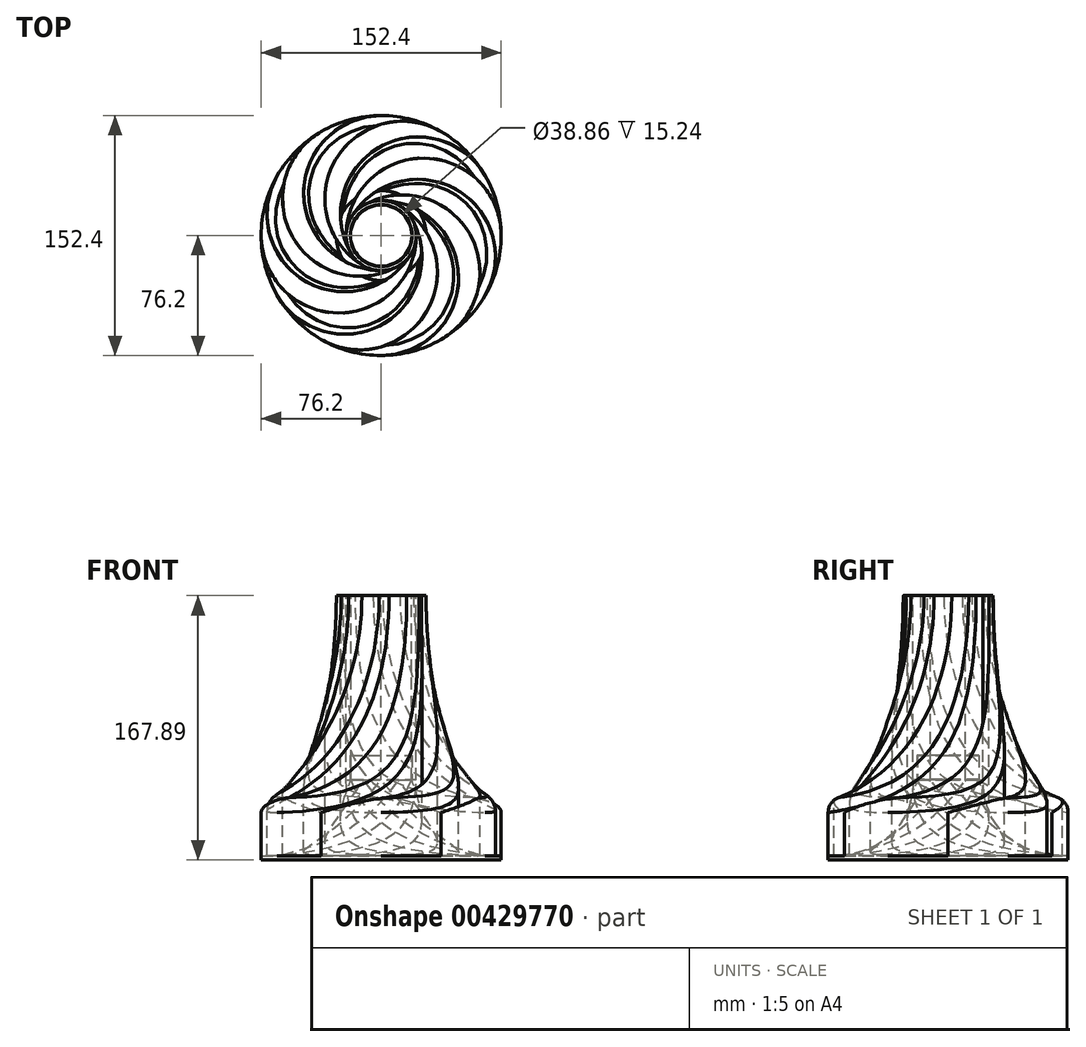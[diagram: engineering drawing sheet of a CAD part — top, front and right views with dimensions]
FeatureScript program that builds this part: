
annotation { "Feature Type Name" : "Feature", "Feature Type Description" : "" }
export const myFeature = defineFeature(function(context is Context, id is Id, definition is map)
    precondition{}
    {
        {
            var Q0;
            Q0=qCreatedBy(makeId("Front.planeOp"),FACE);
            var sketch = newSketch(context, id + "F0", { "sketchPlane" : qUnion([Q0])});
            skLineSegment(sketch, "E0", {"start": v(0, 0) * mm, "end": v(19.68, 0) * mm});
            skLineSegment(sketch, "E1", {"start": v(0, 0) * mm, "end": v(-19.69, 0) * mm});
            skLineSegment(sketch, "E2", {"start": v(19.68, 0) * mm, "end": v(19.68, 15.5) * mm});
            skLineSegment(sketch, "E3", {"start": v(-19.69, 0) * mm, "end": v(-19.69, 15.5) * mm});
            skLineSegment(sketch, "E4", {"start": v(19.68, 15.5) * mm, "end": v(19.43, 15.5) * mm});
            skLineSegment(sketch, "E5", {"start": v(0, 0) * mm, "end": v(0, 0.25) * mm});
            skLineSegment(sketch, "E6", {"start": v(0, 0.25) * mm, "end": v(19.43, 0.25) * mm});
            skLineSegment(sketch, "E7", {"start": v(19.43, 0.25) * mm, "end": v(19.43, 15.5) * mm});
            skLineSegment(sketch, "E8", {"start": v(-19.69, 15.5) * mm, "end": v(-19.43, 15.5) * mm});
            skLineSegment(sketch, "E9", {"start": v(-19.43, 15.5) * mm, "end": v(-19.43, 0.25) * mm});
            skLineSegment(sketch, "E10", {"start": v(-19.43, 0.25) * mm, "end": v(0, 0.25) * mm});
            skSolve(sketch);
        }
        {
            var Q0;
            Q0=makeQuery(id+"F0.imprint","IMPRINT",FACE,{"disambiguationData":[TD([[makeQuery(id+"F0.imprint","IMPRINT",EDGE,{"derivedFrom":sQuery(id+"F0.wireOp",EDGE,"E1")}),-1.0]])]});
            var Q1;
            Q1=sQuery(id+"F0.wireOp",EDGE,"E5");
            revolve(context, id + "F1", {"entities" : qUnion([Q0]), "axis" : qUnion([Q1]), "revolveType" : RevolveType.FULL});
        }
        {
            var Q0;
            Q0=qCreatedBy(makeId("Front.planeOp"),FACE);
            var sketch = newSketch(context, id + "F2", { "sketchPlane" : qUnion([Q0])});
            skLineSegment(sketch, "E11.0", {"start": v(-22.23, 0) * mm, "end": v(-22.23, 15.5) * mm});
            skLineSegment(sketch, "E12", {"start": v(-22.23, 0) * mm, "end": v(0, 0) * mm});
            skLineSegment(sketch, "E13", {"start": v(0, 0) * mm, "end": v(0, -50.8) * mm});
            skLineSegment(sketch, "E14", {"start": v(0, -50.8) * mm, "end": v(-76.2, -50.8) * mm});
            skLineSegment(sketch, "E15", {"start": v(-22.23, 15.5) * mm, "end": v(-22.23, 117.1) * mm});
            skLineSegment(sketch, "E16", {"start": v(-22.23, 117.1) * mm, "end": v(-28.58, 117.1) * mm});
            skLineSegment(sketch, "E17", {"start": v(-76.2, -50.8) * mm, "end": v(-76.2, -12.7) * mm});
            skFitSpline(sketch, "E18", {"points": [v(-28.58, 117.1) * mm, v(-76.2, -12.7) * mm], "startDerivative": vector(0, -266.32) * mm, "endDerivative": vector(-55.61, 0) * mm});
            skSolve(sketch);
        }
        {
            var Q0;
            Q0=makeQuery(id+"F2.imprint","IMPRINT",FACE,{"disambiguationData":[TD([[makeQuery(id+"F2.imprint","IMPRINT",EDGE,{"derivedFrom":sQuery(id+"F2.wireOp",EDGE,"E11.0")}),1.0]])]});
            var Q1;
            Q1=sQuery(id+"F2.wireOp",EDGE,"E13");
            revolve(context, id + "F3", {"entities" : qUnion([Q0]), "axis" : qUnion([Q1]), "revolveType" : RevolveType.FULL});
        }
        {
            var Q0;
            Q0=qCreatedBy(makeId("Top.planeOp"),FACE);
            var sketch = newSketch(context, id + "F4", { "sketchPlane" : qUnion([Q0])});
            skCircle(sketch, "E19.0", {"center": v(0, 0) * mm, "radius": 19.69 * mm});
            skCircle(sketch, "E19.1", {"center": v(0, 0) * mm, "radius": 76.2 * mm});
            skCircle(sketch, "E20.0", {"center": v(0, 0) * mm, "radius": 22.23 * mm});
            skArc(sketch, "E21", {"start": v(0, -76.2) * mm, "mid": v(49.21, -26.99) * mm, "end": v(0, 22.22) * mm});
            skArc(sketch, "E22.1.0", {"start": v(-38.1, -66) * mm, "mid": v(29.13, -47.98) * mm, "end": v(11.11, 19.25) * mm});
            skArc(sketch, "E22.2.0", {"start": v(-66, -38.1) * mm, "mid": v(1.23, -56.11) * mm, "end": v(19.25, 11.11) * mm});
            skArc(sketch, "E22.3.0", {"start": v(-76.2, 0) * mm, "mid": v(-26.99, -49.21) * mm, "end": v(22.22, 0) * mm});
            skArc(sketch, "E22.4.0", {"start": v(-66, 38.1) * mm, "mid": v(-47.98, -29.13) * mm, "end": v(19.25, -11.11) * mm});
            skArc(sketch, "E22.5.0", {"start": v(-38.1, 66) * mm, "mid": v(-56.11, -1.23) * mm, "end": v(11.11, -19.25) * mm});
            skArc(sketch, "E22.6.0", {"start": v(0, 76.2) * mm, "mid": v(-49.21, 26.99) * mm, "end": v(0, -22.22) * mm});
            skArc(sketch, "E22.7.0", {"start": v(38.1, 66) * mm, "mid": v(-29.13, 47.98) * mm, "end": v(-11.11, -19.25) * mm});
            skArc(sketch, "E22.8.0", {"start": v(66, 38.1) * mm, "mid": v(-1.23, 56.11) * mm, "end": v(-19.25, -11.11) * mm});
            skArc(sketch, "E22.9.0", {"start": v(76.2, 0) * mm, "mid": v(26.99, 49.21) * mm, "end": v(-22.22, 0) * mm});
            skArc(sketch, "E22.10.0", {"start": v(66, -38.1) * mm, "mid": v(47.98, 29.13) * mm, "end": v(-19.25, 11.11) * mm});
            skArc(sketch, "E22.11.0", {"start": v(38.1, -66) * mm, "mid": v(56.11, 1.23) * mm, "end": v(-11.11, 19.25) * mm});
            skLineSegment(sketch, "E22.anchor1", {"start": v(0, 0) * mm, "end": v(0, -76.2) * mm, "construction": true});
            skLineSegment(sketch, "E22.anchor2", {"start": v(0, 0) * mm, "end": v(0, -76.2) * mm, "construction": true});
            skSolve(sketch);
        }
        {
            var Q0;
            {var subQ0=sQuery(id+"F4.wireOp",EDGE,"E22.1.0");Q0=makeQuery(id+"F4.imprint","IMPRINT",FACE,{"disambiguationData":[TD([[makeQuery(id+"F4.imprint","IMPRINT",EDGE,{"derivedFrom":subQ0}),1.0]])]});}
            var Q1;
            {var subQ0=sQuery(id+"F4.wireOp",EDGE,"E22.11.0");Q1=makeQuery(id+"F4.imprint","IMPRINT",FACE,{"disambiguationData":[TD([[makeQuery(id+"F4.imprint","IMPRINT",EDGE,{"derivedFrom":subQ0}),1.0]])]});}
            var Q2;
            {var subQ0=sQuery(id+"F4.wireOp",EDGE,"E22.9.0");Q2=makeQuery(id+"F4.imprint","IMPRINT",FACE,{"disambiguationData":[TD([[makeQuery(id+"F4.imprint","IMPRINT",EDGE,{"derivedFrom":subQ0}),1.0]])]});}
            var Q3;
            {var subQ0=sQuery(id+"F4.wireOp",EDGE,"E22.7.0");Q3=makeQuery(id+"F4.imprint","IMPRINT",FACE,{"disambiguationData":[TD([[makeQuery(id+"F4.imprint","IMPRINT",EDGE,{"derivedFrom":subQ0}),1.0]])]});}
            var Q4;
            {var subQ0=sQuery(id+"F4.wireOp",EDGE,"E22.5.0");Q4=makeQuery(id+"F4.imprint","IMPRINT",FACE,{"disambiguationData":[TD([[makeQuery(id+"F4.imprint","IMPRINT",EDGE,{"derivedFrom":subQ0}),1.0]])]});}
            var Q5;
            {var subQ0=sQuery(id+"F4.wireOp",EDGE,"E22.3.0");Q5=makeQuery(id+"F4.imprint","IMPRINT",FACE,{"disambiguationData":[TD([[makeQuery(id+"F4.imprint","IMPRINT",EDGE,{"derivedFrom":subQ0}),1.0]])]});}
            extrude(context, id + "F5", {"entities" : qUnion([Q0, Q1, Q2, Q3, Q4, Q5]), "operationType" : NewBodyOperationType.REMOVE, "endBound" : BoundingType.SYMMETRIC, "oppositeDirection" : true, "depth" : 304.8 * mm});
        }
        {
            var Q0;
            Q0=qCreatedBy(makeId("Front.planeOp"),FACE);
            var sketch = newSketch(context, id + "F6", { "sketchPlane" : qUnion([Q0])});
            skLineSegment(sketch, "E23.0", {"start": v(-22.23, 0) * mm, "end": v(0, 0) * mm});
            skLineSegment(sketch, "E23.1", {"start": v(0, 0) * mm, "end": v(0, -50.8) * mm});
            skLineSegment(sketch, "E23.2", {"start": v(0, -50.8) * mm, "end": v(-76.2, -50.8) * mm});
            skPoint(sketch, "E24", {"position": v(0, -25.4) * mm});
            skLineSegment(sketch, "E25", {"start": v(-76.2, -50.8) * mm, "end": v(-76.2, -48.26) * mm});
            skFitSpline(sketch, "E26", {"points": [v(-22.23, 0) * mm, v(-76.2, -48.26) * mm], "startDerivative": vector(0, -76.2) * mm, "endDerivative": vector(-112.95, 0) * mm});
            skSolve(sketch);
        }
        {
            var Q0;
            Q0=makeQuery(id+"F6.imprint","IMPRINT",FACE,{"disambiguationData":[TD([[makeQuery(id+"F6.imprint","IMPRINT",EDGE,{"derivedFrom":sQuery(id+"F6.wireOp",EDGE,"E23.0")}),-1.0]])]});
            var Q1;
            Q1=sQuery(id+"F6.wireOp",EDGE,"E23.1");
            revolve(context, id + "F7", {"operationType" : NewBodyOperationType.ADD, "entities" : qUnion([Q0]), "axis" : qUnion([Q1]), "revolveType" : RevolveType.FULL});
        }
        {
            var Q0;
            Q0=makeQuery(id+"F5.boolean.opBoolean","INTERSECT",EDGE,{"derivedFrom":[makeQuery(id+"F3.opRevolve","SWEPT_FACE",FACE,{"disambiguationData":[OSD([sQuery(id+"F2.wireOp",EDGE,"E18")])]}),makeQuery(id+"F5.opExtrude","SWEPT_FACE",FACE,{"disambiguationData":[OSD([sQuery(id+"F4.wireOp",EDGE,"E22.4.0")])]})]});
            var Q1;
            Q1=makeQuery(id+"F5.boolean.opBoolean","INTERSECT",EDGE,{"derivedFrom":[makeQuery(id+"F3.opRevolve","SWEPT_FACE",FACE,{"disambiguationData":[OSD([sQuery(id+"F2.wireOp",EDGE,"E18")])]}),makeQuery(id+"F5.opExtrude","SWEPT_FACE",FACE,{"disambiguationData":[OSD([sQuery(id+"F4.wireOp",EDGE,"E22.2.0")])]})]});
            var Q2;
            Q2=makeQuery(id+"F5.boolean.opBoolean","INTERSECT",EDGE,{"derivedFrom":[makeQuery(id+"F3.opRevolve","SWEPT_FACE",FACE,{"disambiguationData":[OSD([sQuery(id+"F2.wireOp",EDGE,"E18")])]}),makeQuery(id+"F5.opExtrude","SWEPT_FACE",FACE,{"disambiguationData":[OSD([sQuery(id+"F4.wireOp",EDGE,"E21")])]})]});
            var Q3;
            Q3=makeQuery(id+"F5.boolean.opBoolean","INTERSECT",EDGE,{"derivedFrom":[makeQuery(id+"F3.opRevolve","SWEPT_FACE",FACE,{"disambiguationData":[OSD([sQuery(id+"F2.wireOp",EDGE,"E18")])]}),makeQuery(id+"F5.opExtrude","SWEPT_FACE",FACE,{"disambiguationData":[OSD([sQuery(id+"F4.wireOp",EDGE,"E22.10.0")])]})]});
            var Q4;
            Q4=makeQuery(id+"F5.boolean.opBoolean","INTERSECT",EDGE,{"derivedFrom":[makeQuery(id+"F3.opRevolve","SWEPT_FACE",FACE,{"disambiguationData":[OSD([sQuery(id+"F2.wireOp",EDGE,"E18")])]}),makeQuery(id+"F5.opExtrude","SWEPT_FACE",FACE,{"disambiguationData":[OSD([sQuery(id+"F4.wireOp",EDGE,"E22.8.0")])]})]});
            var Q5;
            Q5=makeQuery(id+"F5.boolean.opBoolean","INTERSECT",EDGE,{"derivedFrom":[makeQuery(id+"F3.opRevolve","SWEPT_FACE",FACE,{"disambiguationData":[OSD([sQuery(id+"F2.wireOp",EDGE,"E18")])]}),makeQuery(id+"F5.opExtrude","SWEPT_FACE",FACE,{"disambiguationData":[OSD([sQuery(id+"F4.wireOp",EDGE,"E22.6.0")])]})]});
            fillet(context, id + "F8", {"entities" : qUnion([Q0, Q1, Q2, Q3, Q4, Q5]), "radius" : 10.16 * mm, "tangentPropagation" : true, "allowEdgeOverflow" : false});
        }
    });
